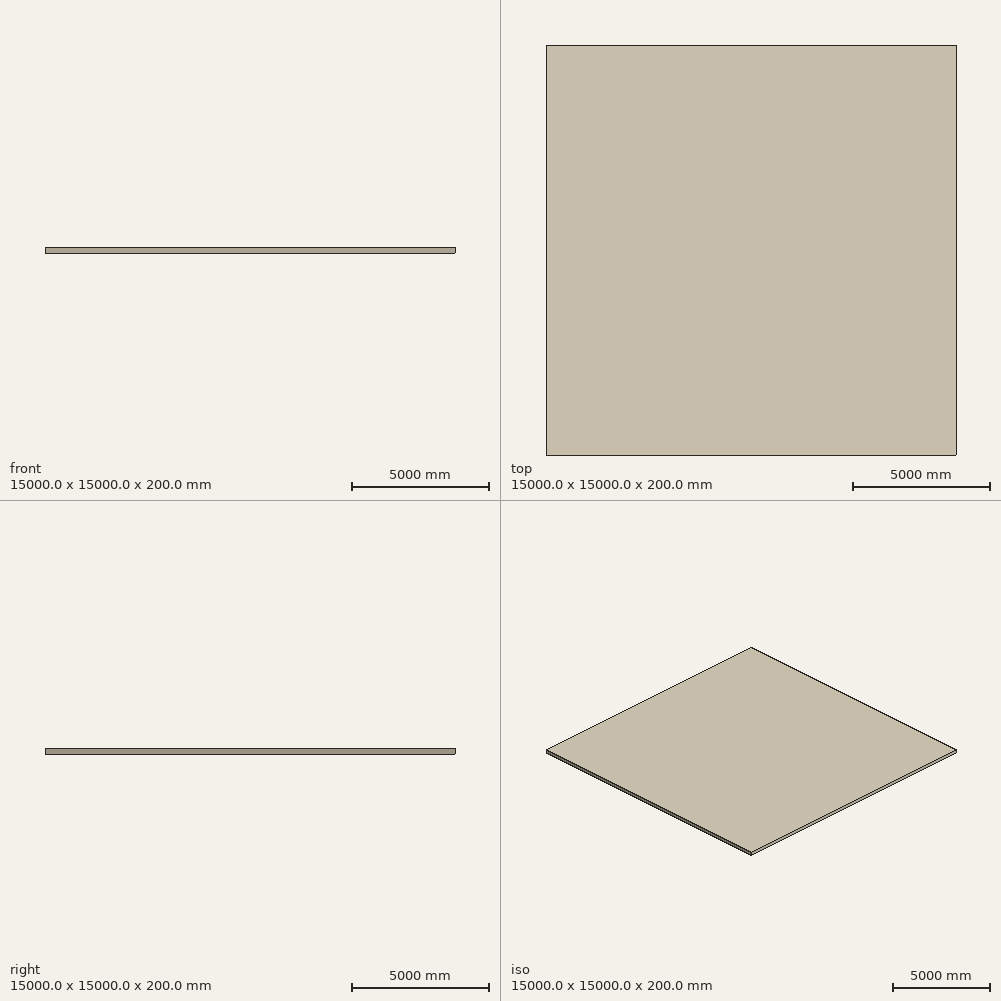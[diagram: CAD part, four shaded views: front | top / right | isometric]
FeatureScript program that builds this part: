
annotation { "Feature Type Name" : "Feature", "Feature Type Description" : "" }
export const myFeature = defineFeature(function(context is Context, id is Id, definition is map)
    precondition{}
    {
        {
            var Q0;
            Q0=qCreatedBy(makeId("Top.planeOp"),FACE);
            var sketch = newSketch(context, id + "F0", { "sketchPlane" : qUnion([Q0])});
            skLineSegment(sketch, "E0.bottom", {"start": v(14955.4, 14956.28) * mm, "end": v(-44.6, 14956.28) * mm});
            skLineSegment(sketch, "E0.top", {"start": v(14955.4, -43.72) * mm, "end": v(-44.6, -43.72) * mm});
            skLineSegment(sketch, "E0.left", {"start": v(14955.4, 14956.28) * mm, "end": v(14955.4, -43.72) * mm});
            skLineSegment(sketch, "E0.right", {"start": v(-44.6, 14956.28) * mm, "end": v(-44.6, -43.72) * mm});
            skSolve(sketch);
        }
        {
            var Q0;
            Q0 = qSketchRegion(id + "F0", true);
            extrude(context, id + "F1", {"entities" : qUnion([Q0]), "depth" : 200 * mm, "offsetDistance" : 25 * mm});
        }
    });
